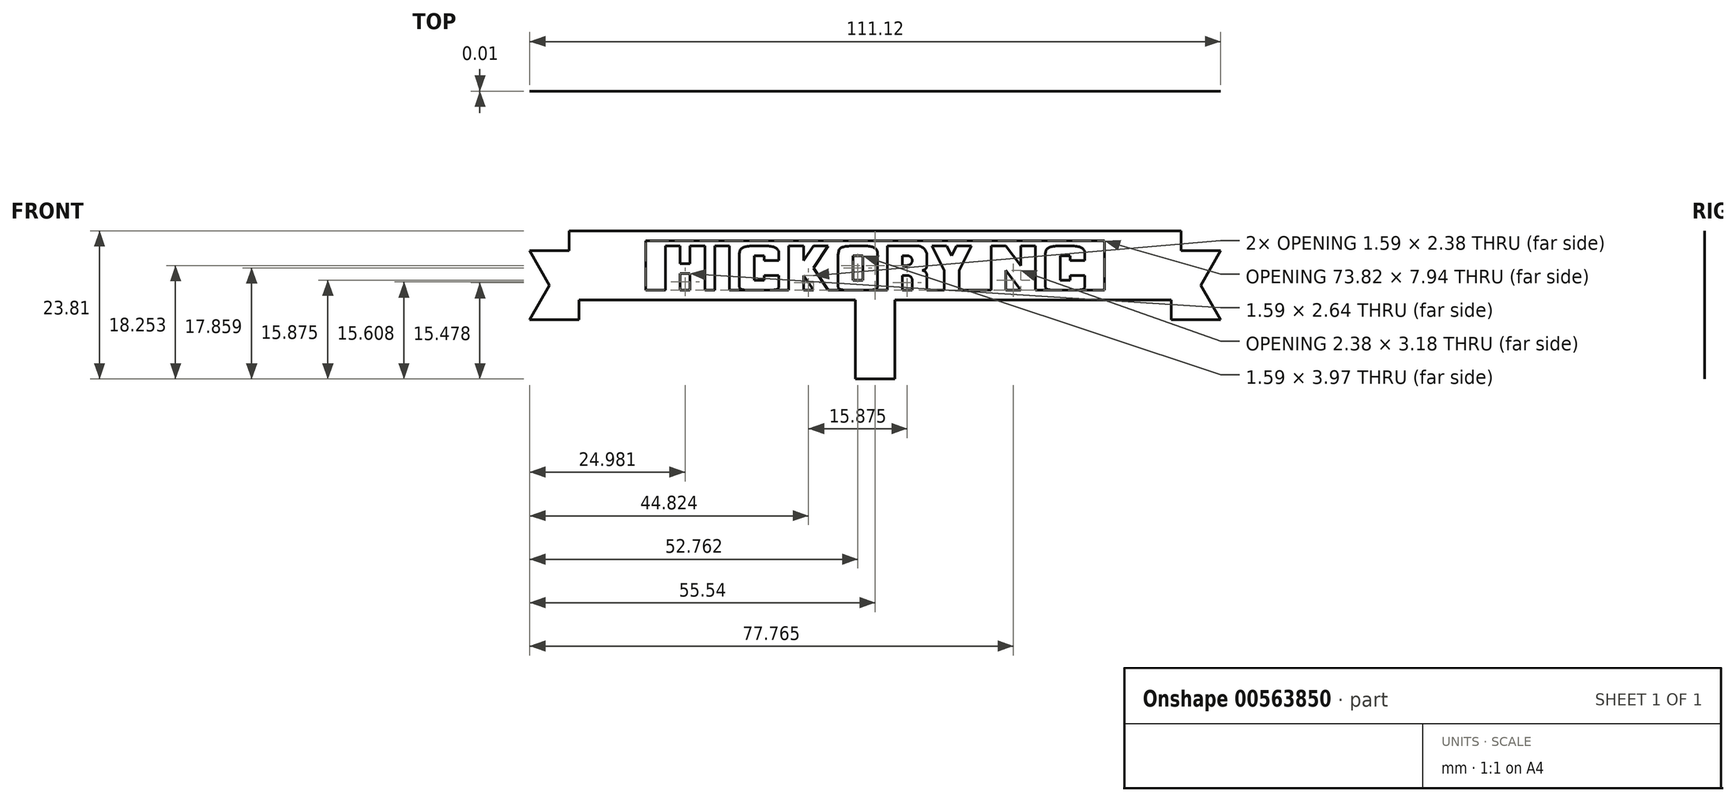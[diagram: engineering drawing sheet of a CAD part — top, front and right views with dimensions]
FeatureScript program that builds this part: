
annotation { "Feature Type Name" : "Feature", "Feature Type Description" : "" }
export const myFeature = defineFeature(function(context is Context, id is Id, definition is map)
    precondition{}
    {
        {
            var Q0;
            Q0=qCreatedBy(makeId("Front.planeOp"),FACE);
            var sketch = newSketch(context, id + "F0", { "sketchPlane" : qUnion([Q0])});
            skLineSegment(sketch, "E0.bottom", {"start": v(55.58, 34.93) * mm, "end": v(-55.54, 34.93) * mm});
            skLineSegment(sketch, "E0.top", {"start": v(55.58, -34.92) * mm, "end": v(-55.54, -34.93) * mm});
            skLineSegment(sketch, "E0.left", {"start": v(55.58, 34.93) * mm, "end": v(55.58, -34.92) * mm});
            skLineSegment(sketch, "E0.right", {"start": v(-55.54, 34.93) * mm, "end": v(-55.54, -34.93) * mm});
            skLineSegment(sketch, "E1", {"start": v(-47.6, -31.75) * mm, "end": v(47.64, -31.75) * mm});
            skLineSegment(sketch, "E2", {"start": v(-47.6, -31.75) * mm, "end": v(-47.6, -34.93) * mm});
            skLineSegment(sketch, "E3", {"start": v(-47.6, -34.93) * mm, "end": v(-55.54, -34.93) * mm});
            skLineSegment(sketch, "E4", {"start": v(-55.54, -34.93) * mm, "end": v(-52.37, -29.37) * mm});
            skLineSegment(sketch, "E5", {"start": v(-52.37, -29.37) * mm, "end": v(-55.54, -23.81) * mm});
            skLineSegment(sketch, "E6", {"start": v(-55.54, -23.81) * mm, "end": v(-49.2, -23.81) * mm});
            skLineSegment(sketch, "E7.bottom", {"start": v(36.9, -22.23) * mm, "end": v(-36.9, -22.23) * mm});
            skLineSegment(sketch, "E7.top", {"start": v(36.9, -30.16) * mm, "end": v(-36.9, -30.16) * mm});
            skLineSegment(sketch, "E7.left", {"start": v(36.9, -22.23) * mm, "end": v(36.9, -30.16) * mm});
            skLineSegment(sketch, "E7.right", {"start": v(-36.9, -22.22) * mm, "end": v(-36.9, -30.16) * mm});
            skPoint(sketch, "E7.middle", {"position": v(0, -26.2) * mm});
            skLineSegment(sketch, "E8", {"start": v(-33.73, -30.16) * mm, "end": v(-33.73, -23.02) * mm});
            skLineSegment(sketch, "E9", {"start": v(-33.73, -23.02) * mm, "end": v(-31.35, -23.02) * mm});
            skLineSegment(sketch, "E10", {"start": v(-31.35, -23.02) * mm, "end": v(-31.35, -25.93) * mm});
            skLineSegment(sketch, "E11", {"start": v(-31.35, -25.93) * mm, "end": v(-29.77, -25.93) * mm});
            skLineSegment(sketch, "E12", {"start": v(-29.77, -25.93) * mm, "end": v(-29.77, -23.02) * mm});
            skLineSegment(sketch, "E13", {"start": v(-29.77, -23.02) * mm, "end": v(-27.38, -23.02) * mm});
            skLineSegment(sketch, "E14", {"start": v(-27.38, -23.02) * mm, "end": v(-27.38, -30.16) * mm});
            skLineSegment(sketch, "E15", {"start": v(-27.38, -30.16) * mm, "end": v(-29.77, -30.16) * mm});
            skLineSegment(sketch, "E16", {"start": v(-29.77, -30.16) * mm, "end": v(-29.77, -27.52) * mm});
            skLineSegment(sketch, "E17", {"start": v(-29.77, -27.52) * mm, "end": v(-31.35, -27.52) * mm});
            skLineSegment(sketch, "E18", {"start": v(-31.35, -27.52) * mm, "end": v(-31.35, -30.16) * mm});
            skLineSegment(sketch, "E19", {"start": v(-31.35, -30.16) * mm, "end": v(-33.73, -30.16) * mm});
            skLineSegment(sketch, "E20", {"start": v(-25.8, -30.16) * mm, "end": v(-25.8, -23.02) * mm});
            skLineSegment(sketch, "E21", {"start": v(-25.8, -23.02) * mm, "end": v(-23.42, -23.02) * mm});
            skLineSegment(sketch, "E22", {"start": v(-23.42, -23.02) * mm, "end": v(-23.42, -30.16) * mm});
            skLineSegment(sketch, "E23", {"start": v(-23.42, -30.16) * mm, "end": v(-25.8, -30.16) * mm});
            skLineSegment(sketch, "E24", {"start": v(-21.83, -30.16) * mm, "end": v(-21.83, -23.02) * mm});
            skLineSegment(sketch, "E25", {"start": v(-21.83, -23.02) * mm, "end": v(-15.48, -23.02) * mm});
            skLineSegment(sketch, "E26", {"start": v(-15.48, -23.02) * mm, "end": v(-15.48, -25.4) * mm});
            skLineSegment(sketch, "E27", {"start": v(-15.48, -25.4) * mm, "end": v(-17.86, -25.4) * mm});
            skLineSegment(sketch, "E28", {"start": v(-17.86, -25.4) * mm, "end": v(-17.86, -24.6) * mm});
            skLineSegment(sketch, "E29", {"start": v(-17.86, -24.6) * mm, "end": v(-19.45, -24.6) * mm});
            skLineSegment(sketch, "E30", {"start": v(-19.45, -24.6) * mm, "end": v(-19.45, -28.57) * mm});
            skLineSegment(sketch, "E31", {"start": v(-19.45, -28.58) * mm, "end": v(-17.86, -28.58) * mm});
            skLineSegment(sketch, "E32", {"start": v(-17.86, -28.57) * mm, "end": v(-17.86, -27.78) * mm});
            skLineSegment(sketch, "E33", {"start": v(-17.86, -27.78) * mm, "end": v(-15.48, -27.78) * mm});
            skLineSegment(sketch, "E34", {"start": v(-15.48, -27.78) * mm, "end": v(-15.48, -30.16) * mm});
            skLineSegment(sketch, "E35", {"start": v(-15.48, -30.16) * mm, "end": v(-21.83, -30.16) * mm});
            skLineSegment(sketch, "E36", {"start": v(-13.9, -30.16) * mm, "end": v(-13.9, -23.02) * mm});
            skLineSegment(sketch, "E37", {"start": v(-13.9, -23.02) * mm, "end": v(-11.5, -23.02) * mm});
            skLineSegment(sketch, "E38", {"start": v(-11.5, -23.02) * mm, "end": v(-11.5, -25.4) * mm});
            skLineSegment(sketch, "E39", {"start": v(-11.5, -25.4) * mm, "end": v(-9.92, -23.02) * mm});
            skLineSegment(sketch, "E40", {"start": v(-9.92, -23.02) * mm, "end": v(-7.54, -23.02) * mm});
            skLineSegment(sketch, "E41", {"start": v(-7.54, -23.02) * mm, "end": v(-9.92, -26.6) * mm});
            skLineSegment(sketch, "E42", {"start": v(-9.92, -26.6) * mm, "end": v(-7.54, -30.16) * mm});
            skLineSegment(sketch, "E43", {"start": v(-7.54, -30.16) * mm, "end": v(-9.92, -30.16) * mm});
            skLineSegment(sketch, "E44", {"start": v(-9.92, -30.16) * mm, "end": v(-11.5, -27.78) * mm});
            skLineSegment(sketch, "E45", {"start": v(-11.5, -27.78) * mm, "end": v(-11.5, -30.16) * mm});
            skLineSegment(sketch, "E46", {"start": v(-11.5, -30.16) * mm, "end": v(-13.9, -30.16) * mm});
            skLineSegment(sketch, "E47", {"start": v(-5.95, -30.16) * mm, "end": v(-5.95, -23.02) * mm});
            skLineSegment(sketch, "E48", {"start": v(-5.95, -23.02) * mm, "end": v(0.4, -23.02) * mm});
            skLineSegment(sketch, "E49", {"start": v(0.4, -23.02) * mm, "end": v(0.4, -30.16) * mm});
            skLineSegment(sketch, "E50", {"start": v(0.4, -30.16) * mm, "end": v(-5.95, -30.16) * mm});
            skLineSegment(sketch, "E51", {"start": v(-3.57, -28.57) * mm, "end": v(-3.57, -24.6) * mm});
            skLineSegment(sketch, "E52", {"start": v(-3.57, -24.6) * mm, "end": v(-1.98, -24.6) * mm});
            skLineSegment(sketch, "E53", {"start": v(-1.98, -24.6) * mm, "end": v(-1.98, -28.57) * mm});
            skLineSegment(sketch, "E54", {"start": v(-1.98, -28.58) * mm, "end": v(-3.57, -28.58) * mm});
            skLineSegment(sketch, "E55", {"start": v(1.98, -30.16) * mm, "end": v(1.98, -23.02) * mm});
            skLineSegment(sketch, "E56", {"start": v(1.98, -23.02) * mm, "end": v(6.75, -23.02) * mm});
            skLineSegment(sketch, "E57", {"start": v(8.33, -24.6) * mm, "end": v(8.33, -26.2) * mm});
            skLineSegment(sketch, "E58", {"start": v(1.98, -30.16) * mm, "end": v(4.37, -30.16) * mm});
            skLineSegment(sketch, "E59", {"start": v(4.37, -30.16) * mm, "end": v(4.37, -27.78) * mm});
            skLineSegment(sketch, "E60", {"start": v(4.37, -27.78) * mm, "end": v(5.16, -27.78) * mm});
            skLineSegment(sketch, "E61", {"start": v(5.95, -28.57) * mm, "end": v(5.95, -30.16) * mm});
            skLineSegment(sketch, "E62", {"start": v(5.95, -30.16) * mm, "end": v(8.33, -30.16) * mm});
            skLineSegment(sketch, "E63", {"start": v(8.33, -30.16) * mm, "end": v(8.33, -27.78) * mm});
            skLineSegment(sketch, "E64", {"start": v(7.54, -26.99) * mm, "end": v(6.75, -26.99) * mm});
            skLineSegment(sketch, "E65", {"start": v(4.37, -24.6) * mm, "end": v(4.37, -26.2) * mm});
            skLineSegment(sketch, "E66", {"start": v(4.37, -26.2) * mm, "end": v(5.16, -26.2) * mm});
            skLineSegment(sketch, "E67", {"start": v(5.95, -25.4) * mm, "end": v(5.95, -25.4) * mm});
            skLineSegment(sketch, "E68", {"start": v(5.16, -24.6) * mm, "end": v(4.37, -24.6) * mm});
            skPoint(sketch, "E69.visualSharp", {"position": v(5.95, -26.2) * mm});
            skArc(sketch, "E69.filletArc", {"start": v(5.16, -26.2) * mm, "mid": v(5.72, -25.96) * mm, "end": v(5.95, -25.4) * mm});
            skPoint(sketch, "E70.visualSharp", {"position": v(5.95, -24.6) * mm});
            skArc(sketch, "E70.filletArc", {"start": v(5.95, -25.4) * mm, "mid": v(5.72, -24.84) * mm, "end": v(5.16, -24.6) * mm});
            skPoint(sketch, "E71.visualSharp", {"position": v(5.95, -27.78) * mm});
            skArc(sketch, "E71.filletArc", {"start": v(5.95, -28.57) * mm, "mid": v(5.72, -28.01) * mm, "end": v(5.16, -27.78) * mm});
            skPoint(sketch, "E72.visualSharp", {"position": v(8.33, -26.99) * mm});
            skArc(sketch, "E72.filletArc", {"start": v(8.33, -27.78) * mm, "mid": v(8.1, -27.22) * mm, "end": v(7.54, -26.99) * mm});
            skArc(sketch, "E73.filletArc", {"start": v(7.54, -26.99) * mm, "mid": v(8.1, -26.76) * mm, "end": v(8.33, -26.2) * mm});
            skArc(sketch, "E74.filletArc", {"start": v(8.33, -24.6) * mm, "mid": v(7.87, -23.48) * mm, "end": v(6.75, -23.02) * mm});
            skLineSegment(sketch, "E75", {"start": v(11.11, -26.99) * mm, "end": v(9.13, -23.02) * mm});
            skLineSegment(sketch, "E76", {"start": v(9.13, -23.02) * mm, "end": v(11.5, -23.02) * mm});
            skLineSegment(sketch, "E77", {"start": v(11.5, -23.02) * mm, "end": v(12.3, -24.6) * mm});
            skLineSegment(sketch, "E78", {"start": v(12.3, -24.6) * mm, "end": v(13.1, -23.02) * mm});
            skLineSegment(sketch, "E79", {"start": v(13.1, -23.02) * mm, "end": v(15.48, -23.02) * mm});
            skLineSegment(sketch, "E80", {"start": v(15.48, -23.02) * mm, "end": v(13.5, -26.99) * mm});
            skLineSegment(sketch, "E81", {"start": v(13.5, -26.99) * mm, "end": v(13.5, -30.16) * mm});
            skLineSegment(sketch, "E82", {"start": v(13.5, -30.16) * mm, "end": v(11.11, -30.16) * mm});
            skLineSegment(sketch, "E83", {"start": v(11.11, -30.16) * mm, "end": v(11.11, -26.99) * mm});
            skLineSegment(sketch, "E84", {"start": v(18.65, -30.16) * mm, "end": v(18.65, -23.02) * mm});
            skLineSegment(sketch, "E85", {"start": v(18.65, -23.02) * mm, "end": v(21.03, -23.02) * mm});
            skLineSegment(sketch, "E86", {"start": v(21.03, -23.02) * mm, "end": v(23.42, -26.2) * mm});
            skLineSegment(sketch, "E87", {"start": v(23.42, -26.2) * mm, "end": v(23.42, -23.02) * mm});
            skLineSegment(sketch, "E88", {"start": v(23.42, -23.02) * mm, "end": v(25.8, -23.02) * mm});
            skLineSegment(sketch, "E89", {"start": v(25.8, -23.02) * mm, "end": v(25.8, -30.16) * mm});
            skLineSegment(sketch, "E90", {"start": v(25.8, -30.16) * mm, "end": v(23.42, -30.16) * mm});
            skLineSegment(sketch, "E91", {"start": v(23.42, -30.16) * mm, "end": v(21.03, -26.99) * mm});
            skLineSegment(sketch, "E92", {"start": v(21.03, -26.99) * mm, "end": v(21.03, -30.16) * mm});
            skLineSegment(sketch, "E93", {"start": v(21.03, -30.16) * mm, "end": v(18.65, -30.16) * mm});
            skLineSegment(sketch, "E94", {"start": v(27.38, -30.16) * mm, "end": v(27.38, -23.02) * mm});
            skLineSegment(sketch, "E95", {"start": v(27.38, -23.02) * mm, "end": v(33.73, -23.02) * mm});
            skLineSegment(sketch, "E96", {"start": v(33.73, -23.02) * mm, "end": v(33.73, -25.4) * mm});
            skLineSegment(sketch, "E97", {"start": v(33.73, -25.4) * mm, "end": v(31.35, -25.4) * mm});
            skLineSegment(sketch, "E98", {"start": v(31.35, -25.4) * mm, "end": v(31.35, -24.6) * mm});
            skLineSegment(sketch, "E99", {"start": v(31.35, -24.6) * mm, "end": v(29.77, -24.6) * mm});
            skLineSegment(sketch, "E100", {"start": v(29.77, -24.6) * mm, "end": v(29.77, -28.57) * mm});
            skLineSegment(sketch, "E101", {"start": v(29.77, -28.58) * mm, "end": v(31.35, -28.58) * mm});
            skLineSegment(sketch, "E102", {"start": v(31.35, -28.57) * mm, "end": v(31.35, -27.78) * mm});
            skLineSegment(sketch, "E103", {"start": v(31.35, -27.78) * mm, "end": v(33.73, -27.78) * mm});
            skLineSegment(sketch, "E104", {"start": v(33.73, -27.78) * mm, "end": v(33.73, -30.16) * mm});
            skLineSegment(sketch, "E105", {"start": v(33.73, -30.16) * mm, "end": v(27.38, -30.16) * mm});
            skLineSegment(sketch, "E106", {"start": v(-49.2, -20.64) * mm, "end": v(49.23, -20.64) * mm});
            skArc(sketch, "E107", {"start": v(-48.44, 34.93) * mm, "mid": v(0, 9.84) * mm, "end": v(48.44, 34.93) * mm});
            skLineSegment(sketch, "E108", {"start": v(47.64, -31.75) * mm, "end": v(47.64, -34.92) * mm});
            skLineSegment(sketch, "E109", {"start": v(47.64, -34.92) * mm, "end": v(55.58, -34.92) * mm});
            skLineSegment(sketch, "E110", {"start": v(55.58, -34.92) * mm, "end": v(52.4, -29.37) * mm});
            skLineSegment(sketch, "E111", {"start": v(52.4, -29.37) * mm, "end": v(55.58, -23.81) * mm});
            skLineSegment(sketch, "E112", {"start": v(55.58, -23.81) * mm, "end": v(49.23, -23.81) * mm});
            skLineSegment(sketch, "E113", {"start": v(49.23, -23.82) * mm, "end": v(49.23, -23.81) * mm});
            skLineSegment(sketch, "E114", {"start": v(49.23, -23.81) * mm, "end": v(49.23, -20.64) * mm});
            skLineSegment(sketch, "E115", {"start": v(-3.16, -31.75) * mm, "end": v(-3.16, -44.45) * mm});
            skLineSegment(sketch, "E116", {"start": v(-3.16, -44.45) * mm, "end": v(3.2, -44.45) * mm});
            skLineSegment(sketch, "E117", {"start": v(3.2, -44.45) * mm, "end": v(3.2, -31.75) * mm});
            skFitSpline(sketch, "E118", {"points": [v(27.38, -24.4) * mm, v(27.58, -23.61) * mm, v(28.18, -23.22) * mm, v(30.56, -23.02) * mm, v(32.94, -23.22) * mm, v(33.54, -23.61) * mm, v(33.73, -24.4) * mm], "startDerivative": vector(0, 8.68) * mm, "endDerivative": vector(0, -8.68) * mm});
            skFitSpline(sketch, "E119", {"points": [v(27.38, -28.77) * mm, v(27.38, -29.57) * mm, v(27.58, -29.96) * mm, v(30.56, -30.16) * mm, v(33.54, -29.96) * mm, v(33.73, -29.57) * mm, v(33.73, -28.77) * mm], "startDerivative": vector(0, -8.78) * mm, "endDerivative": vector(0, 8.78) * mm});
            skFitSpline(sketch, "E120", {"points": [v(-21.83, -24.4) * mm, v(-21.63, -23.61) * mm, v(-21.03, -23.22) * mm, v(-18.65, -23.02) * mm, v(-16.27, -23.22) * mm, v(-15.68, -23.61) * mm, v(-15.48, -24.4) * mm], "startDerivative": vector(0, 8.68) * mm, "endDerivative": vector(0, -8.68) * mm});
            skFitSpline(sketch, "E121", {"points": [v(-21.83, -28.77) * mm, v(-21.83, -29.57) * mm, v(-21.63, -29.96) * mm, v(-18.65, -30.16) * mm, v(-15.68, -29.96) * mm, v(-15.48, -29.57) * mm, v(-15.48, -28.77) * mm], "startDerivative": vector(0, -8.78) * mm, "endDerivative": vector(0, 8.78) * mm});
            skLineSegment(sketch, "E122", {"start": v(-49.2, -23.81) * mm, "end": v(-49.2, -20.64) * mm});
            skFitSpline(sketch, "E123", {"points": [v(-5.95, -24.8) * mm, v(-5.75, -23.61) * mm, v(-5.16, -23.22) * mm, v(-2.78, -23.02) * mm, v(-0.4, -23.22) * mm, v(0.2, -23.61) * mm, v(0.4, -24.4) * mm], "startDerivative": vector(0, 7.36) * mm, "endDerivative": vector(0, -8.93) * mm});
            skFitSpline(sketch, "E124", {"points": [v(-5.95, -28.77) * mm, v(-5.95, -29.57) * mm, v(-5.75, -29.96) * mm, v(-2.78, -30.16) * mm, v(0.2, -29.96) * mm, v(0.4, -29.57) * mm, v(0.4, -28.77) * mm], "startDerivative": vector(0, -8.78) * mm, "endDerivative": vector(0, 8.78) * mm});
            skSolve(sketch);
        }
        {
            var Q0;
            Q0=makeQuery(id+"F0.imprint","IMPRINT",FACE,{"disambiguationData":[TD([[makeQuery(id+"F0.imprint","IMPRINT",EDGE,{"derivedFrom":sQuery(id+"F0.wireOp",EDGE,"E8")}),-1.0]])]});
            var Q1;
            Q1=makeQuery(id+"F0.imprint","IMPRINT",FACE,{"disambiguationData":[TD([[makeQuery(id+"F0.imprint","IMPRINT",EDGE,{"derivedFrom":sQuery(id+"F0.wireOp",EDGE,"E20")}),-1.0]])]});
            var Q2;
            Q2=makeQuery(id+"F0.imprint","IMPRINT",FACE,{"disambiguationData":[TD([[makeQuery(id+"F0.imprint","IMPRINT",EDGE,{"derivedFrom":sQuery(id+"F0.wireOp",EDGE,"E36")}),-1.0]])]});
            var Q3;
            Q3=makeQuery(id+"F0.imprint","IMPRINT",FACE,{"disambiguationData":[TD([[makeQuery(id+"F0.imprint","IMPRINT",EDGE,{"derivedFrom":sQuery(id+"F0.wireOp",EDGE,"E47")}),-1.0]])]});
            var Q4;
            Q4=makeQuery(id+"F0.imprint","IMPRINT",FACE,{"disambiguationData":[TD([[makeQuery(id+"F0.imprint","IMPRINT",EDGE,{"derivedFrom":sQuery(id+"F0.wireOp",EDGE,"E55")}),-1.0]])]});
            var Q5;
            Q5=makeQuery(id+"F0.imprint","IMPRINT",FACE,{"disambiguationData":[TD([[makeQuery(id+"F0.imprint","IMPRINT",EDGE,{"derivedFrom":sQuery(id+"F0.wireOp",EDGE,"E75")}),-1.0]])]});
            var Q6;
            Q6=makeQuery(id+"F0.imprint","IMPRINT",FACE,{"disambiguationData":[TD([[makeQuery(id+"F0.imprint","IMPRINT",EDGE,{"derivedFrom":sQuery(id+"F0.wireOp",EDGE,"E84")}),-1.0]])]});
            var Q7;
            {var subQ0=sQuery(id+"F0.wireOp",EDGE,"l0ZIySx0-vg3P-jLgG-fNMB-vb3vmc6OPedm");Q7=makeQuery(id+"F0.imprint","IMPRINT",FACE,{"disambiguationData":[TD([[makeQuery(id+"F0.imprint","IMPRINT",EDGE,{"derivedFrom":subQ0}),-1.0]])]});}
            var Q8;
            {var subQ3=sQuery(id+"F0.wireOp",EDGE,"QKvW9wcu-P8lc-havp-USbf-cngSFUrBQebI");Q8=makeQuery(id+"F0.imprint","IMPRINT",FACE,{"disambiguationData":[TD([[makeQuery(id+"F0.imprint","IMPRINT",EDGE,{"derivedFrom":subQ3}),-1.0]])]});}
            var Q9;
            {var subQ0=sQuery(id+"F0.wireOp",EDGE,"DXzGiHDl-fEia-vayr-rSGx-CfIsMqx9LyU5");Q9=makeQuery(id+"F0.imprint","IMPRINT",FACE,{"disambiguationData":[TD([[makeQuery(id+"F0.imprint","IMPRINT",EDGE,{"derivedFrom":subQ0}),-1.0]])]});}
            var Q10;
            {var subQ3=sQuery(id+"F0.wireOp",EDGE,"i7U0R7jH-L2wl-5mhq-fjXl-IL0sbYHIAivR");Q10=makeQuery(id+"F0.imprint","IMPRINT",FACE,{"disambiguationData":[TD([[makeQuery(id+"F0.imprint","IMPRINT",EDGE,{"derivedFrom":subQ3}),-1.0]])]});}
            var Q11;
            {var subQ0=sQuery(id+"F0.wireOp",EDGE,"DakkSgFL-HyMu-RR9u-CpqV-3EhFrNYaC1sK");Q11=makeQuery(id+"F0.imprint","IMPRINT",FACE,{"disambiguationData":[TD([[makeQuery(id+"F0.imprint","IMPRINT",EDGE,{"derivedFrom":subQ0}),1.0]])]});}
            var Q12;
            {var subQ23=sQuery(id+"F0.wireOp",EDGE,"E2");Q12=makeQuery(id+"F0.imprint","IMPRINT",FACE,{"disambiguationData":[TD([[makeQuery(id+"F0.imprint","IMPRINT",EDGE,{"derivedFrom":subQ23}),-1.0]])]});}
            var Q13;
            {var subQ0=sQuery(id+"F0.wireOp",EDGE,"E117");var subQ1=sQuery(id+"F0.wireOp",EDGE,"E0.top");var subQ2=makeQuery(id+"F0.imprint","INTERSECT",VERTEX,{"derivedFrom":[subQ1,subQ0]});Q13=makeQuery(id+"F0.imprint","IMPRINT",FACE,{"disambiguationData":[TD([[makeQuery(id+"F0.imprint","IMPRINT",EDGE,{"disambiguationData":[TD([[subQ2,-1.0]])],"derivedFrom":subQ1}),-1.0]])]});}
            var Q14;
            {var subQ5=sQuery(id+"F0.wireOp",EDGE,"E116");Q14=makeQuery(id+"F0.imprint","IMPRINT",FACE,{"disambiguationData":[TD([[makeQuery(id+"F0.imprint","IMPRINT",EDGE,{"derivedFrom":subQ5}),1.0]])]});}
            var Q15;
            Q15=makeQuery(id+"F0.imprint","IMPRINT",FACE,{"disambiguationData":[TD([[makeQuery(id+"F0.imprint","IMPRINT",EDGE,{"derivedFrom":sQuery(id+"F0.wireOp",EDGE,"ovGi5kfO-QFmj-Ssrd-fCUQ-s4tFt1upb0GM")}),-1.0]])]});
            var Q16;
            {var subQ8=sQuery(id+"F0.wireOp",EDGE,"4AW3FDOs-IfRs-DpMF-slZw-YYgJg8lbFtcB");Q16=makeQuery(id+"F0.imprint","IMPRINT",FACE,{"disambiguationData":[TD([[makeQuery(id+"F0.imprint","IMPRINT",EDGE,{"derivedFrom":subQ8}),-1.0]])]});}
            var Q17;
            Q17=makeQuery(id+"F0.imprint","IMPRINT",FACE,{"disambiguationData":[TD([[makeQuery(id+"F0.imprint","IMPRINT",EDGE,{"derivedFrom":sQuery(id+"F0.wireOp",EDGE,"JUU38CtC-USzA-xtvU-Vsjb-EHwFlWhLT8pG")}),-1.0]])]});
            var Q18;
            {var subQ12=sQuery(id+"F0.wireOp",EDGE,"E27");Q18=makeQuery(id+"F0.imprint","IMPRINT",FACE,{"disambiguationData":[TD([[makeQuery(id+"F0.imprint","IMPRINT",EDGE,{"derivedFrom":subQ12}),-1.0]])]});}
            var Q19;
            {var subQ8=sQuery(id+"F0.wireOp",EDGE,"E97");Q19=makeQuery(id+"F0.imprint","IMPRINT",FACE,{"disambiguationData":[TD([[makeQuery(id+"F0.imprint","IMPRINT",EDGE,{"derivedFrom":subQ8}),-1.0]])]});}
            var Q20;
            {var subQ1=sQuery(id+"F0.wireOp",EDGE,"iMe6vJv7-zc8W-7Xaj-qrES-XHXeKSJBXJ29");Q20=makeQuery(id+"F0.imprint","IMPRINT",FACE,{"disambiguationData":[TD([[makeQuery(id+"F0.imprint","IMPRINT",EDGE,{"derivedFrom":subQ1}),-1.0]])]});}
            var Q21;
            {var subQ7=sQuery(id+"F0.wireOp",EDGE,"af21e7a8-155b-4c75-ae5e-4e6390e5e65e");Q21=makeQuery(id+"F0.imprint","IMPRINT",FACE,{"disambiguationData":[TD([[makeQuery(id+"F0.imprint","IMPRINT",EDGE,{"derivedFrom":subQ7}),1.0]])]});}
            var Q22;
            {var subQ1=sQuery(id+"F0.wireOp",EDGE,"4txc4yRy-J8wP-Mkca-UGOd-R3jyYX7m6giZ");Q22=makeQuery(id+"F0.imprint","IMPRINT",FACE,{"disambiguationData":[TD([[makeQuery(id+"F0.imprint","IMPRINT",EDGE,{"derivedFrom":subQ1}),1.0]])]});}
            extrude(context, id + "F1", {"entities" : qUnion([Q0, Q1, Q2, Q3, Q4, Q5, Q6, Q7, Q8, Q9, Q10, Q11, Q12, Q13, Q14, Q15, Q16, Q17, Q18, Q19, Q20, Q21, Q22]), "depth" : 1 / 101.6 * mm, "offsetDistance" : 25.4 * mm});
        }
    });
